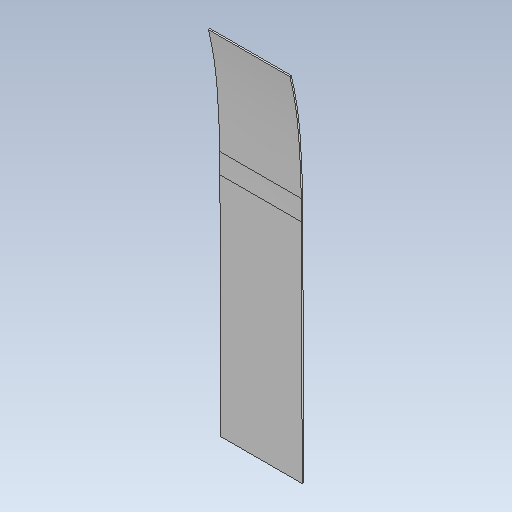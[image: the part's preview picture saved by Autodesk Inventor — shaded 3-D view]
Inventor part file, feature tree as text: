
AUTODESK INVENTOR PART (.ipt)
format: ipt  version: 2020.3 (Build 243373010, 373A)  size: 116,224 bytes
history: native  units: mm
features: other x4, plane x2, sketch x2, sweep x1
ambient origin geometry x8: Origin, YZ Plane, XZ Plane, XY Plane, X Axis, Y Axis, Z Axis, Center Point
bodies: Solid1 (feature_tree)
feature tree (9):
  other  "bottom_offset_wall.ipt"
  other  "base_sketch.ipt"
  plane  "Work Plane1"
  sketch  "Sketch4"  dims[d0=10.0mm d1=10.0mm]
  plane  "Work Plane2"
  sweep  "Sweep1"
  other  "profile"
  other  "bulkhead_main"
  sketch  "Sketch5"  dims[d4=1.2mm d5=1.2mm d6=34.758mm d7=34.758mm d8=0.0mm d9=0.0mm]
